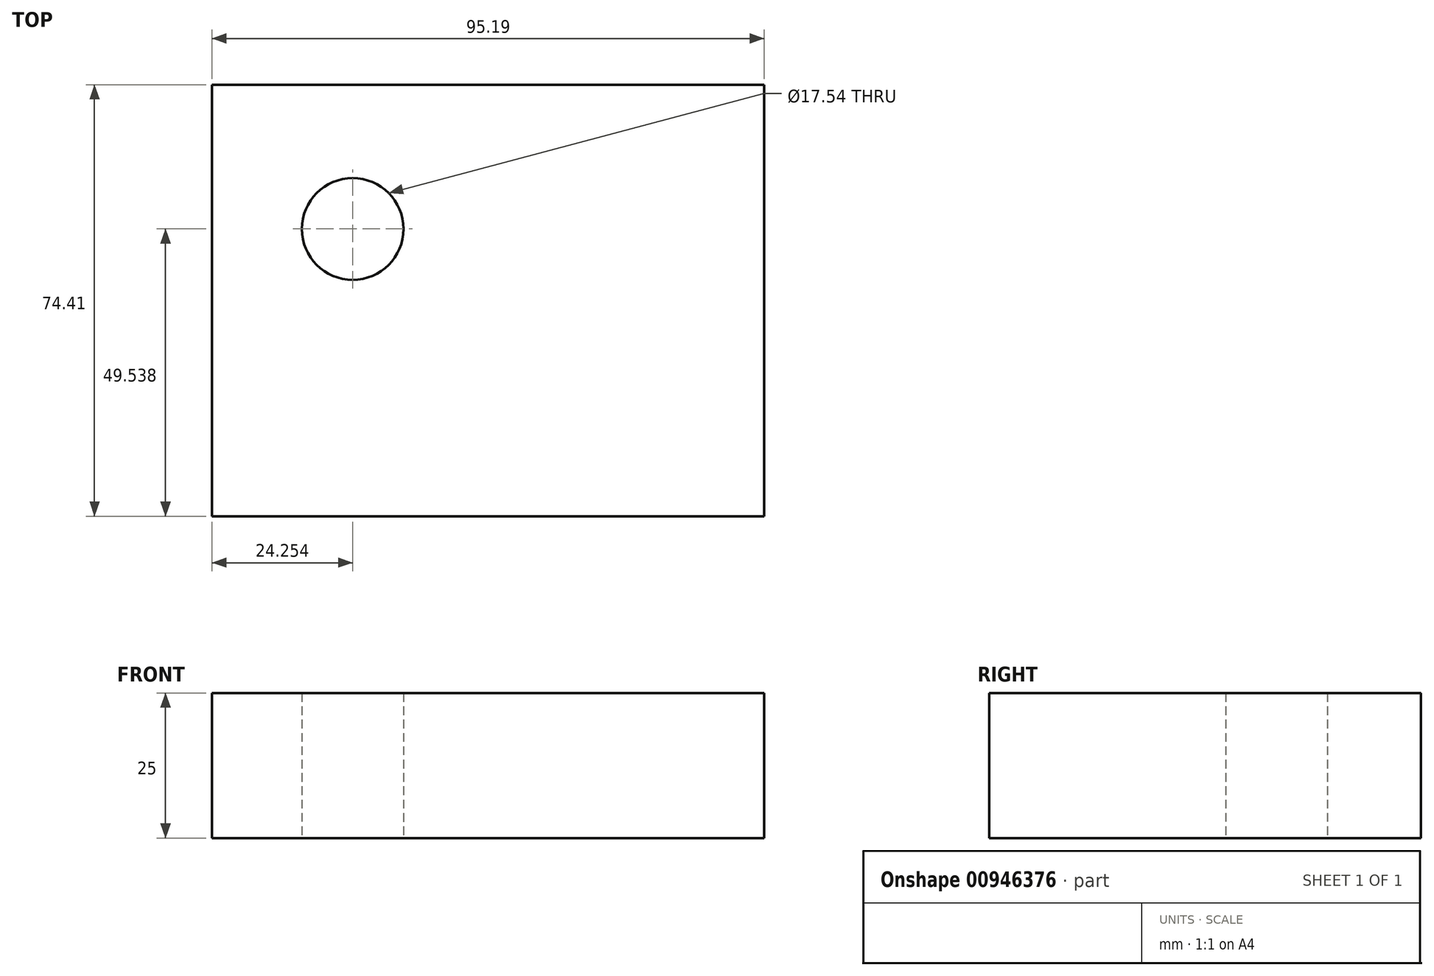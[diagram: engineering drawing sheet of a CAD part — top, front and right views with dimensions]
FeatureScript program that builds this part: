
annotation { "Feature Type Name" : "Feature", "Feature Type Description" : "" }
export const myFeature = defineFeature(function(context is Context, id is Id, definition is map)
    precondition{}
    {
        {
            var Q0;
            Q0=qCreatedBy(makeId("Top.planeOp"),FACE);
            var sketch = newSketch(context, id + "F0", { "sketchPlane" : qUnion([Q0])});
            skLineSegment(sketch, "E0.bottom", {"start": v(-45.76, 33.23) * mm, "end": v(49.43, 33.23) * mm});
            skLineSegment(sketch, "E0.top", {"start": v(-45.76, -41.18) * mm, "end": v(49.43, -41.18) * mm});
            skLineSegment(sketch, "E0.left", {"start": v(-45.76, 33.23) * mm, "end": v(-45.76, -41.18) * mm});
            skLineSegment(sketch, "E0.right", {"start": v(49.43, 33.23) * mm, "end": v(49.43, -41.18) * mm});
            skCircle(sketch, "E1", {"center": v(-21.5, 8.36) * mm, "radius": 8.77 * mm});
            skSolve(sketch);
        }
        {
            var Q0;
            Q0 = qSketchRegion(id + "F0", true);
            extrude(context, id + "F1", {"entities" : qUnion([Q0]), "depth" : 25 * mm, "offsetDistance" : 25 * mm});
        }
    });
